# Revit family: Electrical_Equipment-Floor_Box-Hubbell_Wiring-Single_Service_Metal_Concrete-B2503
name_source: partatom
category: Electrical Fixtures
revit_build: Autodesk Revit 2015 (Build: 20140606_1530(x64)
units: mm (PartAtom-declared; Revit-internal decimal feet)

## types (1)
- B2503 - Brass Collar - 0.75in Access
    Assembly Code = D5020115
    Box Material = Metal-Hubbell-Cast Iron
    Collar Material = Metal-Hubbell-Brass
    Conduit Connector 1 Radius = 0' - 0 3/8"
    Conduit Connector_1 Description = Conduit 0.75in. Connection
    Conduit Connector_2 Description = Conduit 0.75in. Connection
    Conduit Connector_3 Description = Conduit 0.75in. Connection
    Conduit Connector_4 Description = Conduit 0.75in. Connection
    Default Elevation = 0' - 0"
    Description = Flush Round Single-Service Metal Concrete Floor Box
    Floor Box Type = Metal Concrete Floor Box : B2503 - Metal Concrete Floor Box
    Manufacturer = Hubbell-Wiring
    Model = B2503
    Product Documentation Link = http://ecatalog.hubbell-wiring.com
    Product Page URL = http://ecatalog.hubbell-wiring.com
    Product data url = https://bimobject.com
    URL = http://www.hubbell-wiring.com

## geometry (parser evidence)
native form markers: Blend x24, Sweep x10
no freeform markers — native parametric forms only
